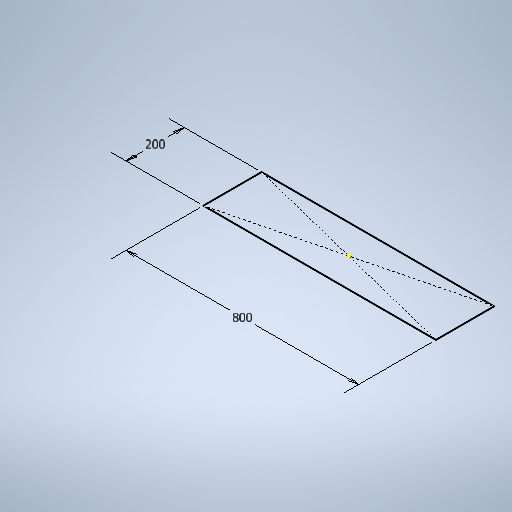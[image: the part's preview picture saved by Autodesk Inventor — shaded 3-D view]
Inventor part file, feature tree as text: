
AUTODESK INVENTOR PART (.ipt)
format: ipt  version: 2025 (Build 290162010, 162A)  size: 250,368 bytes
history: native  units: mm
features: sketch x1
ambient origin geometry x8: Origin, YZ Plane, XZ Plane, XY Plane, X Axis, Y Axis, Z Axis, Center Point
feature tree (1):
  sketch  "Sketch1"  dims[d0=800.0mm d1=200.0mm]
